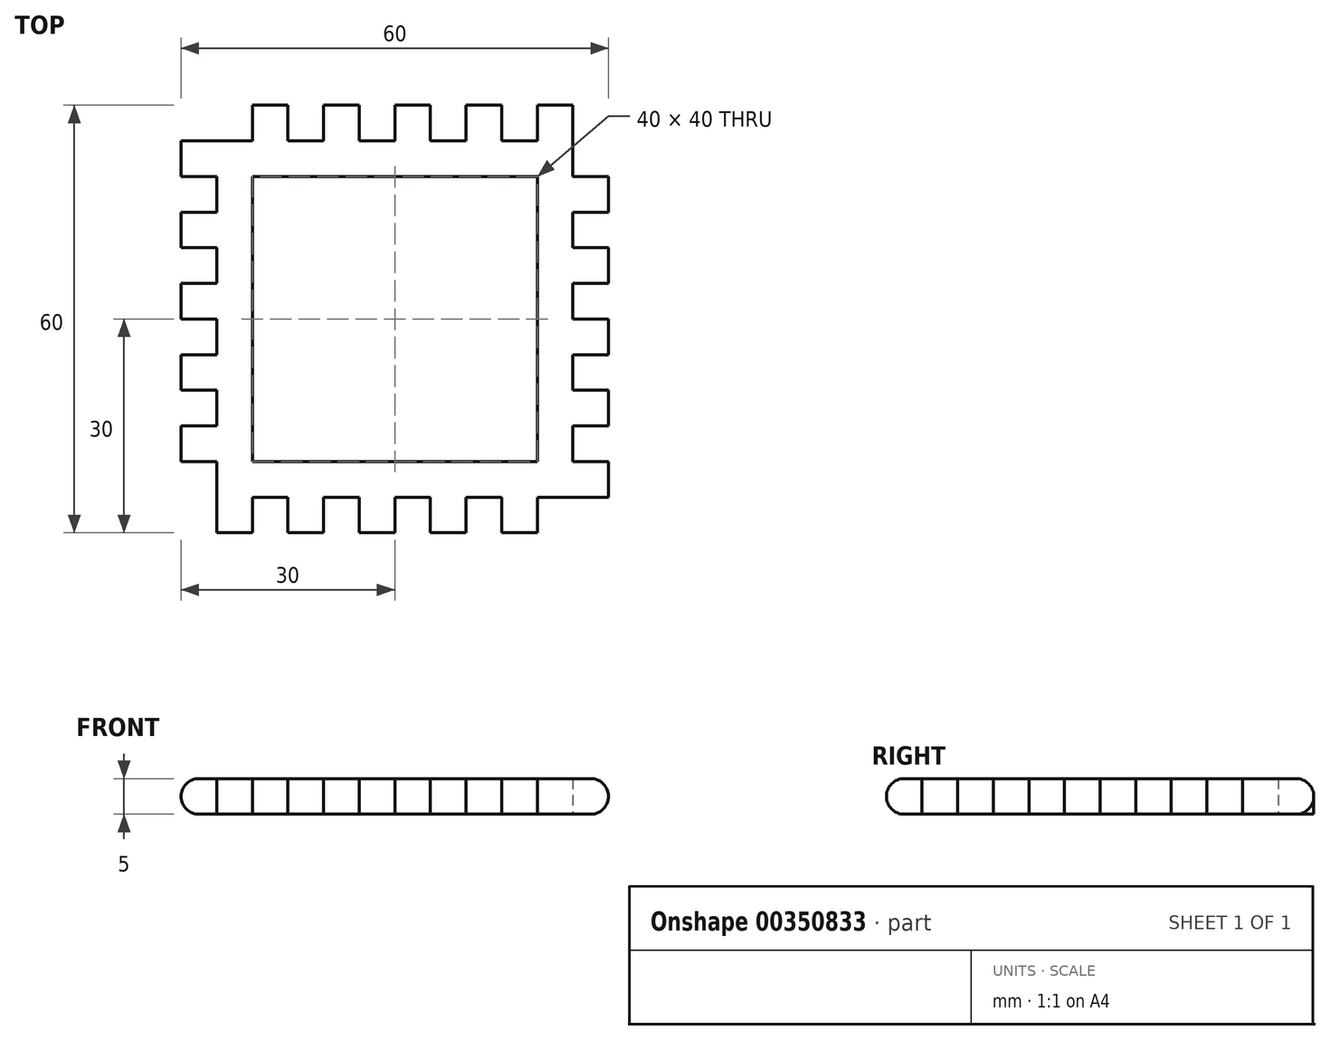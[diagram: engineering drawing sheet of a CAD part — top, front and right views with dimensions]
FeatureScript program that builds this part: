
annotation { "Feature Type Name" : "Feature", "Feature Type Description" : "" }
export const myFeature = defineFeature(function(context is Context, id is Id, definition is map)
    precondition{}
    {
        {
            var Q0;
            Q0=qCreatedBy(makeId("Top.planeOp"),FACE);
            var sketch = newSketch(context, id + "F0", { "sketchPlane" : qUnion([Q0])});
            skLineSegment(sketch, "E0.bottom", {"start": v(25, 25) * mm, "end": v(-25, 25) * mm});
            skLineSegment(sketch, "E0.top", {"start": v(25, -25) * mm, "end": v(-25, -25) * mm});
            skLineSegment(sketch, "E0.left", {"start": v(25, 25) * mm, "end": v(25, -25) * mm});
            skLineSegment(sketch, "E0.right", {"start": v(-25, 25) * mm, "end": v(-25, -25) * mm});
            skPoint(sketch, "E0.middle", {"position": v(0, 0) * mm});
            skLineSegment(sketch, "E1.bottom", {"start": v(-25, -25) * mm, "end": v(-20, -25) * mm});
            skLineSegment(sketch, "E1.top", {"start": v(-25, -30) * mm, "end": v(-20, -30) * mm});
            skLineSegment(sketch, "E1.left", {"start": v(-25, -25) * mm, "end": v(-25, -30) * mm});
            skLineSegment(sketch, "E1.right", {"start": v(-20, -25) * mm, "end": v(-20, -30) * mm});
            skLineSegment(sketch, "E2.1.0.0", {"start": v(-15, -25) * mm, "end": v(-15, -30) * mm});
            skLineSegment(sketch, "E2.1.0.1", {"start": v(-15, -30) * mm, "end": v(-10, -30) * mm});
            skLineSegment(sketch, "E2.1.0.2", {"start": v(-10, -25) * mm, "end": v(-10, -30) * mm});
            skLineSegment(sketch, "E2.2.0.0", {"start": v(-5, -25) * mm, "end": v(-5, -30) * mm});
            skLineSegment(sketch, "E2.2.0.1", {"start": v(-5, -30) * mm, "end": v(0, -30) * mm});
            skLineSegment(sketch, "E2.2.0.2", {"start": v(0, -25) * mm, "end": v(0, -30) * mm});
            skLineSegment(sketch, "E2.3.0.0", {"start": v(5, -25) * mm, "end": v(5, -30) * mm});
            skLineSegment(sketch, "E2.3.0.1", {"start": v(5, -30) * mm, "end": v(10, -30) * mm});
            skLineSegment(sketch, "E2.3.0.2", {"start": v(10, -25) * mm, "end": v(10, -30) * mm});
            skLineSegment(sketch, "E2.4.0.0", {"start": v(15, -25) * mm, "end": v(15, -30) * mm});
            skLineSegment(sketch, "E2.4.0.1", {"start": v(15, -30) * mm, "end": v(20, -30) * mm});
            skLineSegment(sketch, "E2.4.0.2", {"start": v(20, -25) * mm, "end": v(20, -30) * mm});
            skLineSegment(sketch, "E3.1.0", {"start": v(25, -25) * mm, "end": v(30, -25) * mm});
            skLineSegment(sketch, "E3.1.1", {"start": v(30, -25) * mm, "end": v(30, -20) * mm});
            skLineSegment(sketch, "E3.1.2", {"start": v(25, -20) * mm, "end": v(30, -20) * mm});
            skLineSegment(sketch, "E3.1.3", {"start": v(25, -15) * mm, "end": v(30, -15) * mm});
            skLineSegment(sketch, "E3.1.4", {"start": v(30, -15) * mm, "end": v(30, -10) * mm});
            skLineSegment(sketch, "E3.1.5", {"start": v(25, -10) * mm, "end": v(30, -10) * mm});
            skLineSegment(sketch, "E3.1.6", {"start": v(25, -5) * mm, "end": v(30, -5) * mm});
            skLineSegment(sketch, "E3.1.7", {"start": v(30, -5) * mm, "end": v(30, 0) * mm});
            skLineSegment(sketch, "E3.1.8", {"start": v(25, 0) * mm, "end": v(30, 0) * mm});
            skLineSegment(sketch, "E3.1.9", {"start": v(25, 5) * mm, "end": v(30, 5) * mm});
            skLineSegment(sketch, "E3.1.10", {"start": v(30, 5) * mm, "end": v(30, 10) * mm});
            skLineSegment(sketch, "E3.1.11", {"start": v(25, 10) * mm, "end": v(30, 10) * mm});
            skLineSegment(sketch, "E3.1.12", {"start": v(25, 15) * mm, "end": v(30, 15) * mm});
            skLineSegment(sketch, "E3.1.13", {"start": v(30, 15) * mm, "end": v(30, 20) * mm});
            skLineSegment(sketch, "E3.1.14", {"start": v(25, 20) * mm, "end": v(30, 20) * mm});
            skLineSegment(sketch, "E3.2.0", {"start": v(25, 25) * mm, "end": v(25, 30) * mm});
            skLineSegment(sketch, "E3.2.1", {"start": v(25, 30) * mm, "end": v(20, 30) * mm});
            skLineSegment(sketch, "E3.2.2", {"start": v(20, 25) * mm, "end": v(20, 30) * mm});
            skLineSegment(sketch, "E3.2.3", {"start": v(15, 25) * mm, "end": v(15, 30) * mm});
            skLineSegment(sketch, "E3.2.4", {"start": v(15, 30) * mm, "end": v(10, 30) * mm});
            skLineSegment(sketch, "E3.2.5", {"start": v(10, 25) * mm, "end": v(10, 30) * mm});
            skLineSegment(sketch, "E3.2.6", {"start": v(5, 25) * mm, "end": v(5, 30) * mm});
            skLineSegment(sketch, "E3.2.7", {"start": v(5, 30) * mm, "end": v(0, 30) * mm});
            skLineSegment(sketch, "E3.2.8", {"start": v(0, 25) * mm, "end": v(0, 30) * mm});
            skLineSegment(sketch, "E3.2.9", {"start": v(-5, 25) * mm, "end": v(-5, 30) * mm});
            skLineSegment(sketch, "E3.2.10", {"start": v(-5, 30) * mm, "end": v(-10, 30) * mm});
            skLineSegment(sketch, "E3.2.11", {"start": v(-10, 25) * mm, "end": v(-10, 30) * mm});
            skLineSegment(sketch, "E3.2.12", {"start": v(-15, 25) * mm, "end": v(-15, 30) * mm});
            skLineSegment(sketch, "E3.2.13", {"start": v(-15, 30) * mm, "end": v(-20, 30) * mm});
            skLineSegment(sketch, "E3.2.14", {"start": v(-20, 25) * mm, "end": v(-20, 30) * mm});
            skLineSegment(sketch, "E3.3.0", {"start": v(-25, 25) * mm, "end": v(-30, 25) * mm});
            skLineSegment(sketch, "E3.3.1", {"start": v(-30, 25) * mm, "end": v(-30, 20) * mm});
            skLineSegment(sketch, "E3.3.2", {"start": v(-25, 20) * mm, "end": v(-30, 20) * mm});
            skLineSegment(sketch, "E3.3.3", {"start": v(-25, 15) * mm, "end": v(-30, 15) * mm});
            skLineSegment(sketch, "E3.3.4", {"start": v(-30, 15) * mm, "end": v(-30, 10) * mm});
            skLineSegment(sketch, "E3.3.5", {"start": v(-25, 10) * mm, "end": v(-30, 10) * mm});
            skLineSegment(sketch, "E3.3.6", {"start": v(-25, 5) * mm, "end": v(-30, 5) * mm});
            skLineSegment(sketch, "E3.3.7", {"start": v(-30, 5) * mm, "end": v(-30, 0) * mm});
            skLineSegment(sketch, "E3.3.8", {"start": v(-25, 0) * mm, "end": v(-30, 0) * mm});
            skLineSegment(sketch, "E3.3.9", {"start": v(-25, -5) * mm, "end": v(-30, -5) * mm});
            skLineSegment(sketch, "E3.3.10", {"start": v(-30, -5) * mm, "end": v(-30, -10) * mm});
            skLineSegment(sketch, "E3.3.11", {"start": v(-25, -10) * mm, "end": v(-30, -10) * mm});
            skLineSegment(sketch, "E3.3.12", {"start": v(-25, -15) * mm, "end": v(-30, -15) * mm});
            skLineSegment(sketch, "E3.3.13", {"start": v(-30, -15) * mm, "end": v(-30, -20) * mm});
            skLineSegment(sketch, "E3.3.14", {"start": v(-25, -20) * mm, "end": v(-30, -20) * mm});
            skLineSegment(sketch, "E4.0", {"start": v(20, 20) * mm, "end": v(-20, 20) * mm});
            skLineSegment(sketch, "E4.1", {"start": v(20, 20) * mm, "end": v(20, -20) * mm});
            skLineSegment(sketch, "E4.2", {"start": v(20, -20) * mm, "end": v(-20, -20) * mm});
            skLineSegment(sketch, "E4.3", {"start": v(-20, 20) * mm, "end": v(-20, -20) * mm});
            skSolve(sketch);
        }
        {
            var Q0;
            Q0 = qSketchRegion(id + "F0", true);
            extrude(context, id + "F1", {"entities" : qUnion([Q0]), "depth" : 5 * mm});
        }
        {
            var Q0;
            Q0=makeQuery(id+"F1.opExtrude","CAP_EDGE",EDGE,{"disambiguationData":[OSD([sQuery(id+"F0.wireOp",EDGE,"E3.3.1")])],"isStart":false});
            var Q1;
            Q1=makeQuery(id+"F1.opExtrude","CAP_EDGE",EDGE,{"disambiguationData":[OSD([sQuery(id+"F0.wireOp",EDGE,"E3.3.1")])],"isStart":true});
            var Q2;
            Q2=makeQuery(id+"F1.opExtrude","CAP_EDGE",EDGE,{"disambiguationData":[OSD([sQuery(id+"F0.wireOp",EDGE,"E3.3.4")])],"isStart":false});
            var Q3;
            Q3=makeQuery(id+"F1.opExtrude","CAP_EDGE",EDGE,{"disambiguationData":[OSD([sQuery(id+"F0.wireOp",EDGE,"E3.3.4")])],"isStart":true});
            var Q4;
            Q4=makeQuery(id+"F1.opExtrude","CAP_EDGE",EDGE,{"disambiguationData":[OSD([sQuery(id+"F0.wireOp",EDGE,"E3.3.7")])],"isStart":true});
            var Q5;
            Q5=makeQuery(id+"F1.opExtrude","CAP_EDGE",EDGE,{"disambiguationData":[OSD([sQuery(id+"F0.wireOp",EDGE,"E3.3.7")])],"isStart":false});
            var Q6;
            Q6=makeQuery(id+"F1.opExtrude","CAP_EDGE",EDGE,{"disambiguationData":[OSD([sQuery(id+"F0.wireOp",EDGE,"E3.3.10")])],"isStart":true});
            var Q7;
            Q7=makeQuery(id+"F1.opExtrude","CAP_EDGE",EDGE,{"disambiguationData":[OSD([sQuery(id+"F0.wireOp",EDGE,"E3.3.10")])],"isStart":false});
            var Q8;
            Q8=makeQuery(id+"F1.opExtrude","CAP_EDGE",EDGE,{"disambiguationData":[OSD([sQuery(id+"F0.wireOp",EDGE,"E3.3.13")])],"isStart":false});
            var Q9;
            Q9=makeQuery(id+"F1.opExtrude","CAP_EDGE",EDGE,{"disambiguationData":[OSD([sQuery(id+"F0.wireOp",EDGE,"E3.3.13")])],"isStart":true});
            var Q10;
            Q10=makeQuery(id+"F1.opExtrude","CAP_EDGE",EDGE,{"disambiguationData":[OSD([sQuery(id+"F0.wireOp",EDGE,"E1.top")])],"isStart":false});
            var Q11;
            Q11=makeQuery(id+"F1.opExtrude","CAP_EDGE",EDGE,{"disambiguationData":[OSD([sQuery(id+"F0.wireOp",EDGE,"E1.top")])],"isStart":true});
            var Q12;
            Q12=makeQuery(id+"F1.opExtrude","CAP_EDGE",EDGE,{"disambiguationData":[OSD([sQuery(id+"F0.wireOp",EDGE,"E2.1.0.1")])],"isStart":false});
            var Q13;
            Q13=makeQuery(id+"F1.opExtrude","CAP_EDGE",EDGE,{"disambiguationData":[OSD([sQuery(id+"F0.wireOp",EDGE,"E2.1.0.1")])],"isStart":true});
            var Q14;
            Q14=makeQuery(id+"F1.opExtrude","CAP_EDGE",EDGE,{"disambiguationData":[OSD([sQuery(id+"F0.wireOp",EDGE,"E2.2.0.1")])],"isStart":true});
            var Q15;
            Q15=makeQuery(id+"F1.opExtrude","CAP_EDGE",EDGE,{"disambiguationData":[OSD([sQuery(id+"F0.wireOp",EDGE,"E2.2.0.1")])],"isStart":false});
            var Q16;
            Q16=makeQuery(id+"F1.opExtrude","CAP_EDGE",EDGE,{"disambiguationData":[OSD([sQuery(id+"F0.wireOp",EDGE,"E2.3.0.1")])],"isStart":false});
            var Q17;
            Q17=makeQuery(id+"F1.opExtrude","CAP_EDGE",EDGE,{"disambiguationData":[OSD([sQuery(id+"F0.wireOp",EDGE,"E2.3.0.1")])],"isStart":true});
            var Q18;
            Q18=makeQuery(id+"F1.opExtrude","CAP_EDGE",EDGE,{"disambiguationData":[OSD([sQuery(id+"F0.wireOp",EDGE,"E2.4.0.1")])],"isStart":true});
            var Q19;
            Q19=makeQuery(id+"F1.opExtrude","CAP_EDGE",EDGE,{"disambiguationData":[OSD([sQuery(id+"F0.wireOp",EDGE,"E2.4.0.1")])],"isStart":false});
            var Q20;
            Q20=makeQuery(id+"F1.opExtrude","CAP_EDGE",EDGE,{"disambiguationData":[OSD([sQuery(id+"F0.wireOp",EDGE,"E3.1.1")])],"isStart":false});
            var Q21;
            Q21=makeQuery(id+"F1.opExtrude","CAP_EDGE",EDGE,{"disambiguationData":[OSD([sQuery(id+"F0.wireOp",EDGE,"E3.1.1")])],"isStart":true});
            var Q22;
            Q22=makeQuery(id+"F1.opExtrude","CAP_EDGE",EDGE,{"disambiguationData":[OSD([sQuery(id+"F0.wireOp",EDGE,"E3.1.4")])],"isStart":false});
            var Q23;
            Q23=makeQuery(id+"F1.opExtrude","CAP_EDGE",EDGE,{"disambiguationData":[OSD([sQuery(id+"F0.wireOp",EDGE,"E3.1.4")])],"isStart":true});
            var Q24;
            Q24=makeQuery(id+"F1.opExtrude","CAP_EDGE",EDGE,{"disambiguationData":[OSD([sQuery(id+"F0.wireOp",EDGE,"E3.1.7")])],"isStart":false});
            var Q25;
            Q25=makeQuery(id+"F1.opExtrude","CAP_EDGE",EDGE,{"disambiguationData":[OSD([sQuery(id+"F0.wireOp",EDGE,"E3.1.7")])],"isStart":true});
            var Q26;
            Q26=makeQuery(id+"F1.opExtrude","CAP_EDGE",EDGE,{"disambiguationData":[OSD([sQuery(id+"F0.wireOp",EDGE,"E3.1.10")])],"isStart":false});
            var Q27;
            Q27=makeQuery(id+"F1.opExtrude","CAP_EDGE",EDGE,{"disambiguationData":[OSD([sQuery(id+"F0.wireOp",EDGE,"E3.1.10")])],"isStart":true});
            var Q28;
            Q28=makeQuery(id+"F1.opExtrude","CAP_EDGE",EDGE,{"disambiguationData":[OSD([sQuery(id+"F0.wireOp",EDGE,"E3.1.13")])],"isStart":false});
            var Q29;
            Q29=makeQuery(id+"F1.opExtrude","CAP_EDGE",EDGE,{"disambiguationData":[OSD([sQuery(id+"F0.wireOp",EDGE,"E3.1.13")])],"isStart":true});
            var Q30;
            Q30=makeQuery(id+"F1.opExtrude","CAP_EDGE",EDGE,{"disambiguationData":[OSD([sQuery(id+"F0.wireOp",EDGE,"E3.2.1")])],"isStart":false});
            var Q31;
            Q31=makeQuery(id+"F1.opExtrude","CAP_EDGE",EDGE,{"disambiguationData":[OSD([sQuery(id+"F0.wireOp",EDGE,"E3.2.1")])],"isStart":true});
            var Q32;
            Q32=makeQuery(id+"F1.opExtrude","CAP_EDGE",EDGE,{"disambiguationData":[OSD([sQuery(id+"F0.wireOp",EDGE,"E3.2.4")])],"isStart":false});
            var Q33;
            Q33=makeQuery(id+"F1.opExtrude","CAP_EDGE",EDGE,{"disambiguationData":[OSD([sQuery(id+"F0.wireOp",EDGE,"E3.2.7")])],"isStart":false});
            var Q34;
            Q34=makeQuery(id+"F1.opExtrude","CAP_EDGE",EDGE,{"disambiguationData":[OSD([sQuery(id+"F0.wireOp",EDGE,"E3.2.7")])],"isStart":true});
            var Q35;
            Q35=makeQuery(id+"F1.opExtrude","CAP_EDGE",EDGE,{"disambiguationData":[OSD([sQuery(id+"F0.wireOp",EDGE,"E3.2.10")])],"isStart":false});
            var Q36;
            Q36=makeQuery(id+"F1.opExtrude","CAP_EDGE",EDGE,{"disambiguationData":[OSD([sQuery(id+"F0.wireOp",EDGE,"E3.2.10")])],"isStart":true});
            var Q37;
            Q37=makeQuery(id+"F1.opExtrude","CAP_EDGE",EDGE,{"disambiguationData":[OSD([sQuery(id+"F0.wireOp",EDGE,"E3.2.13")])],"isStart":false});
            var Q38;
            Q38=makeQuery(id+"F1.opExtrude","CAP_EDGE",EDGE,{"disambiguationData":[OSD([sQuery(id+"F0.wireOp",EDGE,"E3.2.13")])],"isStart":true});
            fillet(context, id + "F2", {"entities" : qUnion([Q0, Q1, Q2, Q3, Q4, Q5, Q6, Q7, Q8, Q9, Q10, Q11, Q12, Q13, Q14, Q15, Q16, Q17, Q18, Q19, Q20, Q21, Q22, Q23, Q24, Q25, Q26, Q27, Q28, Q29, Q30, Q31, Q32, Q33, Q34, Q35, Q36, Q37, Q38]), "radius" : 2.5 * mm, "tangentPropagation" : true, "allowEdgeOverflow" : false});
        }
    });
